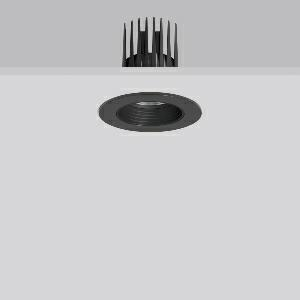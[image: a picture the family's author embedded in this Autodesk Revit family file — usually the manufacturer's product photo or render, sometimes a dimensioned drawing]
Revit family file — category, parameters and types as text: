
# Revit family: heledon_mini_e_901743_003_2_fa16
name_source: partatom
category: Lighting Fixtures
units: mm (PartAtom-declared; Revit-internal decimal feet)

## family parameters
Cut with Voids When Loaded = No
Host = Face
Light Source = No
Part Type = Normal
Room Calculation Point = No
Round Connector Dimension = Use Diameter
Shared = No

## types (1)
- HELEDON mini E (1 x LED Modul 927, 2100 lm, 2700)
    Apparent Load = 20 VA
    Approval mark = CE
    CIE Flux Codes = 99 100 100 100 100
    Color Rendering = 92
    Color Temperature = 2700
    Default Elevation = 1800 mm
    Description = Series: HELEDON mini
Round recessed downlight. Housing: die-cast aluminium, powder-coated. Black plastic ring and recessed LED to prevent glare from the side. Optical assembly with lens made of plastic (polycarbonate) for the best homogeneous light distribution - can be changed without tools. Best colour rendering index Ra>90. Suitable for Recessed ceiling mounting. Installation without tools thanks to spring fastening system. Including separate LED converter with connecting cable 600 mm.High quality converter without flickering and stroboscopic effect. Through-wiring box (5 pole) available as accessory. The following accessories can be mounted without use of tools: interchangeable lenses, decorative glasses, honeycomb louvre, clear and frosted diffusers, white interchangeable plastic ring. 
Colour: deep black, matt (RAL 9005)
Diameter: 124 mm
Height: 3 mm
Cut-out diameter: 114 mm
Recess height: 170 mm
Luminaire: recess height: 120 mm
Lamp: LED
Socket: without socket
Colour temperature: 2700K
Colour rendering index (CRI): 92
System power: 20 W
Rated luminous flux: 2100 lm
Luminous efficiency: 105 lm/W
Control gear: Regulated power supply
Protection class: II
Type of protection: IP 20
    Height = 0 mm  [stored 0 ft]
    Lamp = 1 x LED Modul 927
    Lamp Light Flux = 2100 lm
    Lamp count = 1
    Length = 124 mm  [stored 0.406824 ft]
    Lifetime = 50000 h
    Luminous efficacy = 105 lm/W
    Manufacturer = RZB
    ModVariant = No
    Model = 901743.003.2
    Mounting Place = Ceiling
    Mounting Type = Recessed
    Number of Poles = 1
    OnlyDefault = Yes
    Power Factor = 1
    Product Name = HELEDON mini E
    Product group = Recessed downlights
    ProductGroupID = 402
    Protection Class = Protection class II
    Protection Degree = IP 20
    RLX_Detail_Level = 1
    RLX_Emergency_Light_Flux = 0 lm
    RLX_Emergency_Type = 0
    RLX_Emergency_Type_DB = No
    RlxData = <blob elided: 123441 chars, md5=6d882d0d>
    Socket = socket
    Standby Power = 0 W
    System Light Flux = 2100 lm
    System Power = 20 W
    Type Comments = Product without accessories
    Type Image = 901656.003.jpg
    URL = http://relux.com
    VarID = ---
    Voltage = 230 V
    Voltage Range = 220-240 V
    Weight = 0.00 kg
    Width = 0 mm  [stored 0 ft]

note: [stored X ft] marks values corroborated as IEEE doubles in the binary element streams (Revit-internal decimal feet)

## geometry (parser evidence)
native form markers: Blend x4, Sweep x12
no freeform markers — native parametric forms only
